# Revit family: PRD_AR_ShwrThrmsttcVlvs_ThermostaticSingle-leverWall-mountedMixer_F4LT2003
name_source: partatom
category: Plumbing Fixtures
units: mm (PartAtom-declared; Revit-internal decimal feet)

## family parameters
Cut with Voids When Loaded = Yes
Host = Face
OmniClass Number = 23.45.55.17
OmniClass Title = Mixing Faucets
Part Type = Normal
Room Calculation Point = No
Round Connector Dimension = Use Diameter
Shared = No

## types (1)
- F4LT2003
    AccentColour = none
    AdditionalConnections = no
    AssetType = Fixed
    BIMObjectName = PRD_AR_ShowerThermostaticValves_ThermostaticSingle-leverWall-mountedMixer_F4LT2003
    BasicColour = chrome-look (glossy)
    BodyMaterial = PRD_AR_ChromatedBrass_HighPolished
    Category = Pr_40_20_87_80, Shower thermostatic valves
    Circulation = no
    CloseOffRating = 0.0 Pa
    Color = chrome-look (glossy)
    CompatibleA3000Open = no
    ConnectionWithPayWaterDispenser = not possible
    Default Elevation = 1219 mm
    Description = F4LT-Med thermostatic single lever mixer as DN 15 wall-mounted mixer for wall mounting, for shower facilities in the healthcare and nursing sectors, with 118 mm lever. Thermostat-controlled mixer cartridge with expansion element and active scald protection, fail-safe against backflow as well as adjustable and turn-proof temperature stop, and ceramic disc technology. Without additional backflow preventer for optimised drinking water hygiene. Lever cap with an ergonomic bracket design and slight curvature in the front with basalt-grey coating, in line with two-senses principle (tactile and visual). For connection to hot and cold water. Tap optimised for cleaning, scald-protected, safe-touch housing with hand shower connection, G 1/2 B. All-metal construction, polished chromium-plated brass. Decoupled from the tap housing, volume-reduced, smooth water flow from low-lead brass (lead proportion ≤ 0.2%), and without nickel coating. With thermal insulation components to reduce heat transfer from the tap housing to the cold-water line.With adjustable and lockable connections with strainers, fully covered by depth-adjustable screw rosettes.
    DiameterNominal = 15  [stored 0.0492126 ft]
    DurationUnit = year
    Features = For connection to hot water and cold water. With hand shower connection.
    Finish = polished chrome-plated
    FlowCoefficient = 0
    ForHandShower = yes
    FunctionalPrinciple = manual
    IfcExportAs = IfcValveType
    IfcExportType = MIXING
    InletSize = G 1/2 B
    LockingMechanism = Top section, ceramic
    Manufacturer = KWC Group AG
    ManufacturerName = KWC Group AG
    ManufacturerURL = www.kwc.com
    Material = Brass
    MaterialFitting = brass-look
    MixerControl = LeverHandle
    Model = F4LT2003
    ModelNumber = 2030066757
    ModelReference = F4LT2003
    NBSDescription = Shower mixers
    NBSReference = 45-35-70/335
    Name = F4LT-Med thermostatic single-lever wall-mounted mixer with hand shower connection F4LT2003
    NominalDepth = 0 mm  [stored 0 ft]
    NominalHeight = 0 mm  [stored 0 ft]
    NominalWidth = 305 mm  [stored 1.00066 ft]
    OutletConnectionSize = 15 mm  [stored 0.0492126 ft]
    PositionOfWaterConnection = from backside
    ProductInformation = http://pim.kwc.com
    ShowerPipeDraining = no
    Size = 15
    Status = New
    SurfaceFinishFitting = chromed
    SurfaceTreatmentFitting = polished
    TailorMade = no
    TemperatureLimit = yes
    TestPressure = 0.0 Pa
    TypeOfMixing = with thermostat
    TypeOfMounting = wall mounting
    TypeOfOperation = manual operation
    TypeOfShower = wall fitting
    URL = www.kwc.com
    Uniclass2015Code = Pr_40_20_87_80
    Uniclass2015Title = Shower thermostatic valves
    Uniclass2015Version = Products v1.32
    ValveMechanism = OTHER
    ValveOperation = LEVER
    ValvePattern = ANGLED_2_PORT
    Version = 1
    VolumeFlowRate = 0.22 l/s at 3 bar
    WarrantyDurationUnit = year
    WaterConnection = S-unions
    WorkingPressure = 0.0 Pa

note: [stored X ft] marks values corroborated as IEEE doubles in the binary element streams (Revit-internal decimal feet)

## geometry (parser evidence)
native form markers: Sweep x7
no freeform markers — native parametric forms only
